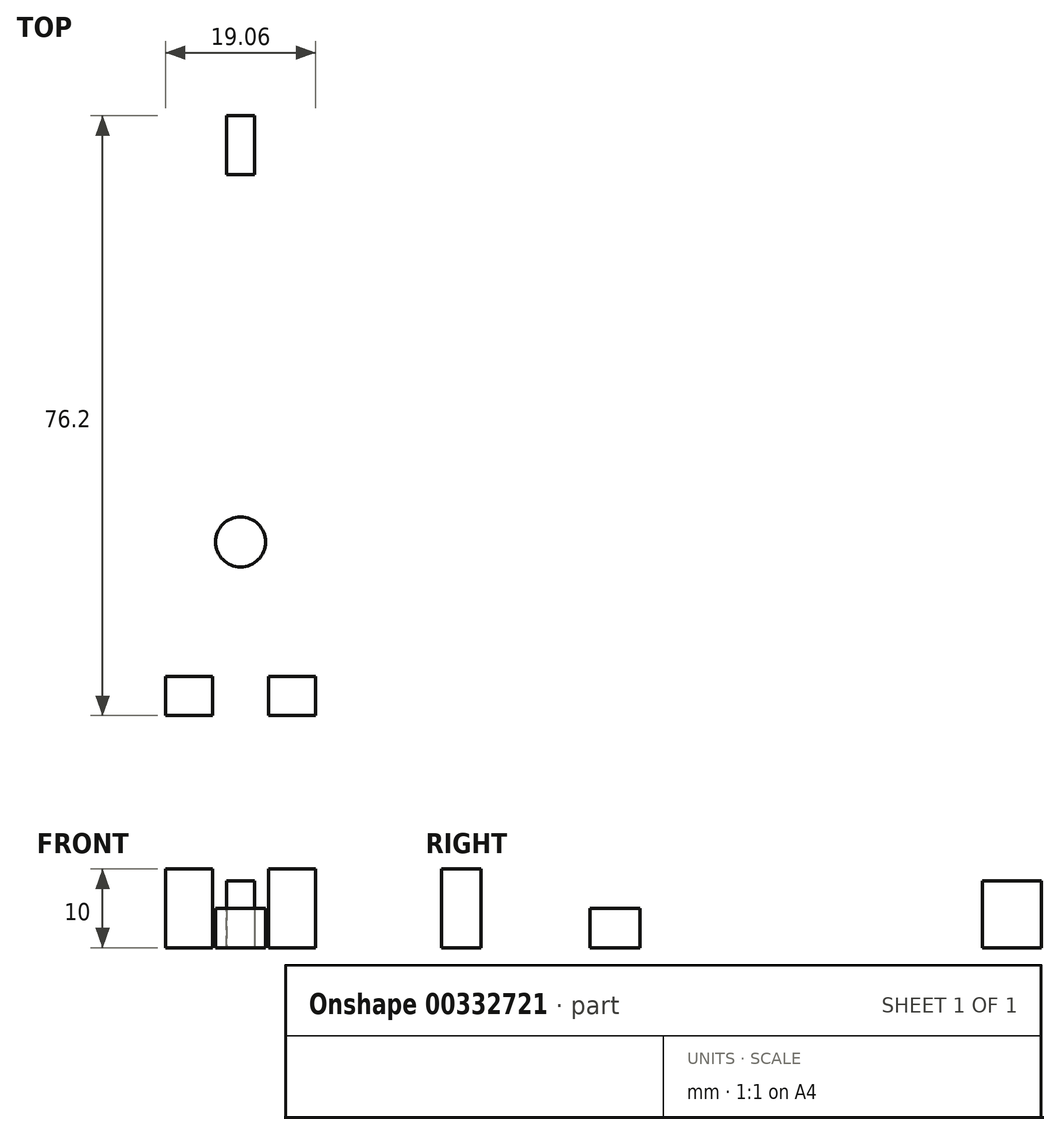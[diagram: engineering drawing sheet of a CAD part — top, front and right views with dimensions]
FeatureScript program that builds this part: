
annotation { "Feature Type Name" : "Feature", "Feature Type Description" : "" }
export const myFeature = defineFeature(function(context is Context, id is Id, definition is map)
    precondition{}
    {
        {
            var Q0;
            Q0=qCreatedBy(makeId("Top.planeOp"),FACE);
            var sketch = newSketch(context, id + "F0", { "sketchPlane" : qUnion([Q0])});
            skLineSegment(sketch, "E0.bottom", {"start": v(-9.52, 38.1) * mm, "end": v(9.53, 38.1) * mm});
            skLineSegment(sketch, "E0.top", {"start": v(-9.53, -38.1) * mm, "end": v(9.52, -38.1) * mm});
            skLineSegment(sketch, "E0.left", {"start": v(-9.52, 38.1) * mm, "end": v(-9.53, -38.1) * mm});
            skLineSegment(sketch, "E0.right", {"start": v(9.53, 38.1) * mm, "end": v(9.52, -38.1) * mm});
            skPoint(sketch, "E0.middle", {"position": v(0, 0) * mm});
            skSolve(sketch);
        }
        {
            var Q0;
            Q0=makeQuery(id+"F0.imprint","IMPRINT",FACE,{"disambiguationData":[TD([[makeQuery(id+"F0.imprint","IMPRINT",EDGE,{"derivedFrom":sQuery(id+"F0.wireOp",EDGE,"E0.bottom")}),-1.0]])]});
            extrude(context, id + "F1", {"entities" : qUnion([Q0]), "depth" : 5 * mm});
        }
        {
            var Q0;
            Q0=makeQuery(id+"F1.opExtrude","CAP_FACE",FACE,{"disambiguationData":[OSD([sQuery(id+"F0.wireOp",EDGE,"E0.bottom"),sQuery(id+"F0.wireOp",EDGE,"E0.top"),sQuery(id+"F0.wireOp",EDGE,"E0.left"),sQuery(id+"F0.wireOp",EDGE,"E0.right")])],"isStart":false});
            var sketch = newSketch(context, id + "F2", { "sketchPlane" : qUnion([Q0])});
            skLineSegment(sketch, "E1.bottom", {"start": v(-9.53, -38.1) * mm, "end": v(-3.53, -38.1) * mm});
            skLineSegment(sketch, "E1.top", {"start": v(-9.53, -33.1) * mm, "end": v(-3.53, -33.1) * mm});
            skLineSegment(sketch, "E1.left", {"start": v(-9.53, -38.1) * mm, "end": v(-9.53, -33.1) * mm});
            skLineSegment(sketch, "E1.right", {"start": v(-3.53, -38.1) * mm, "end": v(-3.53, -33.1) * mm});
            skLineSegment(sketch, "E2.MirrorCS", {"start": v(9.53, -33.1) * mm, "end": v(3.53, -33.1) * mm});
            skLineSegment(sketch, "E3.MirrorCS", {"start": v(3.53, -38.1) * mm, "end": v(3.53, -33.1) * mm});
            skLineSegment(sketch, "E4.bottom", {"start": v(-1.75, 38.1) * mm, "end": v(1.75, 38.1) * mm});
            skLineSegment(sketch, "E4.top", {"start": v(-1.75, 30.6) * mm, "end": v(1.75, 30.6) * mm});
            skLineSegment(sketch, "E4.left", {"start": v(-1.75, 38.1) * mm, "end": v(-1.75, 30.6) * mm});
            skLineSegment(sketch, "E4.right", {"start": v(1.75, 38.1) * mm, "end": v(1.75, 30.6) * mm});
            skPoint(sketch, "E4.middle", {"position": v(0, 34.35) * mm});
            skPoint(sketch, "E4.middle.positionSnap0", {"position": v(0, 38.1) * mm});
            skPoint(sketch, "E4.centerSnap0", {"position": v(0, 38.1) * mm});
            skSolve(sketch);
        }
        {
            var Q0;
            Q0=makeQuery(id+"F2.imprint","IMPRINT",FACE,{"disambiguationData":[TD([[makeQuery(id+"F2.imprint","IMPRINT",EDGE,{"derivedFrom":sQuery(id+"F2.wireOp",EDGE,"E4.bottom")}),-1.0]])]});
            var Q1;
            Q1=makeQuery(id+"F2.imprint","IMPRINT",FACE,{"disambiguationData":[TD([[makeQuery(id+"F2.imprint","IMPRINT",EDGE,{"derivedFrom":sQuery(id+"F2.wireOp",EDGE,"E1.bottom")}),1.0]])]});
            var Q2;
            {var subQ0=sQuery(id+"F2.wireOp",EDGE,"E2.MirrorCS");Q2=makeQuery(id+"F2.imprint","IMPRINT",FACE,{"disambiguationData":[TD([[makeQuery(id+"F2.imprint","IMPRINT",EDGE,{"derivedFrom":subQ0}),1.0]])]});}
            extrude(context, id + "F3", {"entities" : qUnion([Q0, Q1, Q2]), "operationType" : NewBodyOperationType.ADD, "depth" : 5 * mm});
        }
        {
            var Q0;
            Q0=makeQuery(id+"F1.opExtrude","CAP_FACE",FACE,{"disambiguationData":[OSD([sQuery(id+"F0.wireOp",EDGE,"E0.bottom"),sQuery(id+"F0.wireOp",EDGE,"E0.top"),sQuery(id+"F0.wireOp",EDGE,"E0.left"),sQuery(id+"F0.wireOp",EDGE,"E0.right")])],"isStart":false});
            var sketch = newSketch(context, id + "F4", { "sketchPlane" : qUnion([Q0])});
            skCircle(sketch, "E5", {"center": v(0, 16.04) * mm, "radius": 3.18 * mm});
            skLineSegment(sketch, "E6", {"start": v(0, 16.04) * mm, "end": v(0, 0) * mm, "construction": true});
            skCircle(sketch, "E7.MirrorC", {"center": v(0, -16.04) * mm, "radius": 3.18 * mm});
            skSolve(sketch);
        }
        {
            var Q0;
            Q0=makeQuery(id+"F4.imprint","IMPRINT",FACE,{"disambiguationData":[TD([[makeQuery(id+"F4.imprint","IMPRINT",EDGE,{"derivedFrom":sQuery(id+"F4.wireOp",EDGE,"E5")}),1.0]])]});
            var Q1;
            Q1=makeQuery(id+"F4.imprint","IMPRINT",FACE,{"disambiguationData":[TD([[makeQuery(id+"F4.imprint","IMPRINT",EDGE,{"derivedFrom":sQuery(id+"F4.wireOp",EDGE,"E7.MirrorC")}),-1.0]])]});
            extrude(context, id + "F5", {"entities" : qUnion([Q0, Q1]), "operationType" : NewBodyOperationType.REMOVE, "oppositeDirection" : true, "depth" : 5 * mm});
        }
        {
            var Q0;
            Q0=makeQuery(id+"F3.opExtrude","CAP_FACE",FACE,{"disambiguationData":[OSD([sQuery(id+"F2.wireOp",EDGE,"E4.bottom"),sQuery(id+"F2.wireOp",EDGE,"E4.top"),sQuery(id+"F2.wireOp",EDGE,"E4.left"),sQuery(id+"F2.wireOp",EDGE,"E4.right")])],"isStart":false});
            extrude(context, id + "F6", {"entities" : qUnion([Q0]), "operationType" : NewBodyOperationType.REMOVE, "oppositeDirection" : true, "depth" : 1.5 * mm});
        }
    });
